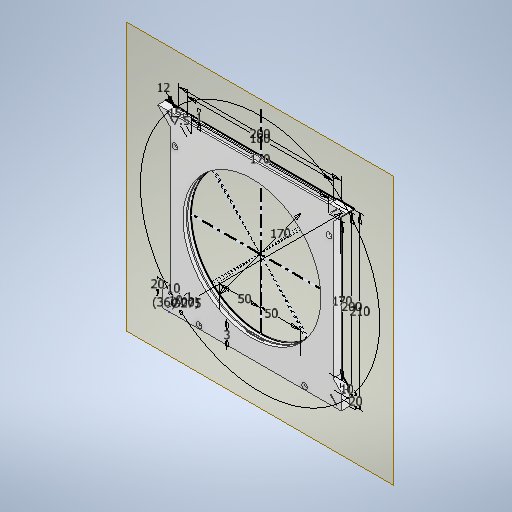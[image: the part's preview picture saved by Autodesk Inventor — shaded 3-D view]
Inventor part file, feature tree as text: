
AUTODESK INVENTOR PART (.ipt)
format: ipt  version: 2025.1 (Build 291241000, 241)  size: 850,944 bytes
history: native  units: mm
features: chamfer x6, extrude x5, sketch x3, other x3, plane x1, hole x1
ambient origin geometry x8: Origin, YZ Plane, XZ Plane, XY Plane, X Axis, Y Axis, Z Axis, Center Point
bodies: Solid1 (feature_tree)
feature tree (19):
  plane  "Work Plane1"
  sketch  "Sketch1"  dims[d0=180.0mm d1=200.0mm]
  extrude  "Extrusion1"  Depth=200.0mm
  extrude  "Extrusion2"  Depth=210.0mm
  extrude  "Extrusion3"  Depth=170.0mm
  chamfer  "Chamfer3"  Distance=50.0mm
  chamfer  "Chamfer4"  Distance=50.0mm
  chamfer  "Chamfer5"  Distance=10.0mm
  chamfer  "Chamfer6"  Distance=4.25mm
  hole  "Hole1"  [1 undecoded]
  extrude  "Extrusion4"  Depth=10.0mm TaperAngle=45.0deg
  extrude  "Extrusion5"  Depth=10.0mm TaperAngle=45.0deg
  chamfer  "Chamfer7"  Distance=0.5mm Angle=45.0deg
  chamfer  "Chamfer8"  Distance=1.0mm Angle=45.0deg
  sketch  "Sketch2"  dims[d4=170.0mm d5=170.0mm d6=50.0mm d7=50.0mm d8=10.0mm d9=0.0mm d10=4.25mm d11=0.0mm d12=4.25mm d13=0.0mm d20=10.0mm d21=1.5mm d22=45.0deg d23=10.0mm d24=1.5mm d25=45.0deg d26=2.0mm d27=0.5mm d28=45.0deg d29=3.0mm d30=1.0mm d31=45.0deg d32=20.0mm d33=10.0mm d34=3.0mm d35=10.0mm d36=20.0mm d38=12.0mm d40=1.0mm d41=35.0mm d42=35.0mm d43=5.0mm d44=180.0mm d45=5.0mm d46=3.797mm d47=6.0mm d48=7.087mm d49=2.0mm d50=14.3117mm d51=8.0mm d52=20.594885mm d53=170.0mm d54=2.0mm d55=0.0mm d56=10.0mm d57=0.0mm d58=2.0mm d59=6.0mm d60=45.0deg d61=2.0mm d62=6.0mm d63=45.0deg d65=10.0mm d66=40.0mm d68=360.0deg d70=275.0mm d71=4.0mm d72=1.0mm d73=15.0mm d74=7.5mm]
  sketch  "Sketch Circular Pattern1"  dims[d2=200.0mm d3=210.0mm]
  parser-record x1  (decoder bookkeeping rows leaked as tree rows — omitted from the tree; the rows remain in map.json)
  other  "Target Holder With Sensors.iam"
  other  "Front Plate:1"
note: 1 required parameter value undecoded (feature->parameter linkage not recoverable at this tier; creation-order binding heuristic only, values carry confidence <= 0.55)
note: 1 file-system path scrubbed to <path> (originals preserved in map.json)
